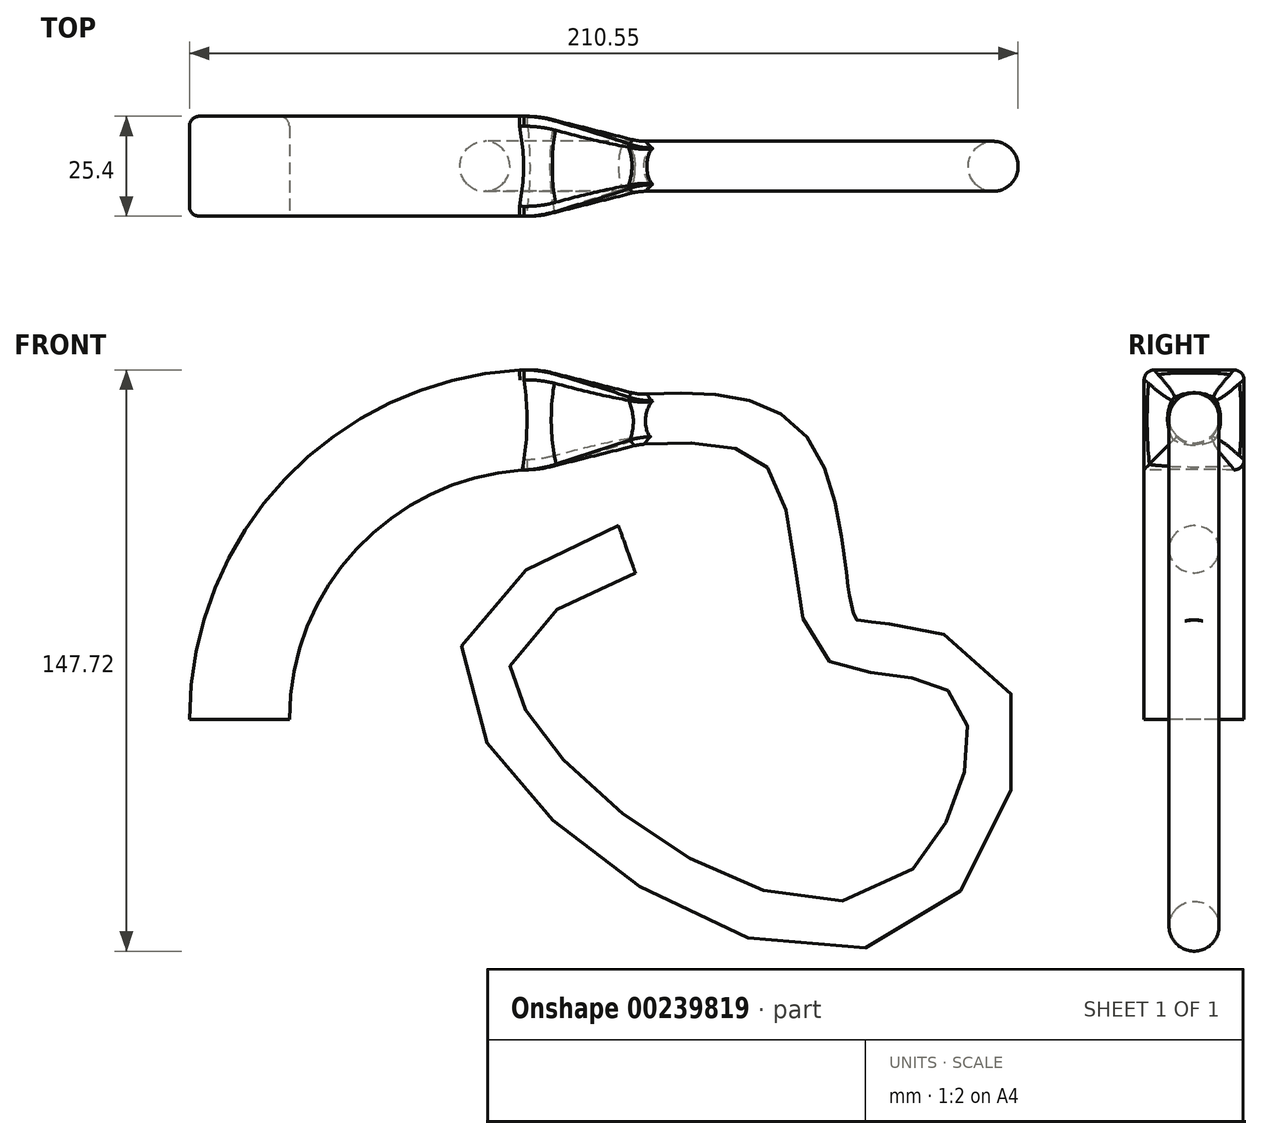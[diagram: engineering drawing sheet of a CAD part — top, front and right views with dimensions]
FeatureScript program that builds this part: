
annotation { "Feature Type Name" : "Feature", "Feature Type Description" : "" }
export const myFeature = defineFeature(function(context is Context, id is Id, definition is map)
    precondition{}
    {
        {
            var Q0;
            Q0=qCreatedBy(makeId("Top.planeOp"),FACE);
            var sketch = newSketch(context, id + "F0", { "sketchPlane" : qUnion([Q0])});
            skLineSegment(sketch, "E0.bottom", {"start": v(12.7, 12.7) * mm, "end": v(-12.7, 12.7) * mm});
            skLineSegment(sketch, "E0.top", {"start": v(12.7, -12.7) * mm, "end": v(-12.7, -12.7) * mm});
            skLineSegment(sketch, "E0.left", {"start": v(12.7, 12.7) * mm, "end": v(12.7, -12.7) * mm});
            skLineSegment(sketch, "E0.right", {"start": v(-12.7, 12.7) * mm, "end": v(-12.7, -12.7) * mm});
            skPoint(sketch, "E0.middle", {"position": v(0, 0) * mm});
            skSolve(sketch);
        }
        {
            var Q0;
            Q0=qCreatedBy(makeId("Front.planeOp"),FACE);
            var sketch = newSketch(context, id + "F1", { "sketchPlane" : qUnion([Q0])});
            skArc(sketch, "E1", {"start": v(76.2, 76.2) * mm, "mid": v(22.32, 53.88) * mm, "end": v(0, 0) * mm});
            skLineSegment(sketch, "E2", {"start": v(0, 0) * mm, "end": v(76.2, 0) * mm, "construction": true});
            skLineSegment(sketch, "E3", {"start": v(76.2, 76.2) * mm, "end": v(76.2, 0) * mm, "construction": true});
            skSolve(sketch);
        }
        {
            var Q0;
            Q0=makeQuery(id+"F0.imprint","IMPRINT",FACE,{"disambiguationData":[TD([[makeQuery(id+"F0.imprint","IMPRINT",EDGE,{"derivedFrom":sQuery(id+"F0.wireOp",EDGE,"E0.bottom")}),1.0]])]});
            var Q1;
            Q1=sQuery(id+"F1.wireOp",EDGE,"E1");
            sweep(context, id + "F2", {"profiles" : qUnion([Q0]), "path" : qUnion([Q1])});
        }
        {
            var Q0;
            Q0=makeQuery(id+"F2.opSweep","CAP_FACE",FACE,{"disambiguationData":[OSD([sQuery(id+"F0.wireOp",EDGE,"E0.bottom"),sQuery(id+"F0.wireOp",EDGE,"E0.top"),sQuery(id+"F0.wireOp",EDGE,"E0.left"),sQuery(id+"F0.wireOp",EDGE,"E0.right"),sQuery(id+"F1.wireOp",VERTEX,"E1.start")])],"isStart":false});
            cPlane(context, id + "F3", {"entities" : qUnion([Q0]), "cplaneType" : CPlaneType.OFFSET, "offset" : 25.4 * mm, "width" : 152.4 * mm, "height" : 152.4 * mm});
        }
        {
            var Q0;
            Q0=qCreatedBy(id+"F3.planeOp",FACE);
            var sketch = newSketch(context, id + "F4", { "sketchPlane" : qUnion([Q0])});
            skCircle(sketch, "E4", {"center": v(0, 76.2) * mm, "radius": 6.35 * mm});
            skLineSegment(sketch, "E5", {"start": v(0, 76.2) * mm, "end": v(12.7, 76.2) * mm, "construction": true});
            skLineSegment(sketch, "E6", {"start": v(0, 76.2) * mm, "end": v(0, 88.9) * mm, "construction": true});
            skSolve(sketch);
        }
        {
            var Q0;
            Q0=makeQuery(id+"F2.opSweep","CAP_FACE",FACE,{"disambiguationData":[OSD([sQuery(id+"F0.wireOp",EDGE,"E0.bottom"),sQuery(id+"F0.wireOp",EDGE,"E0.top"),sQuery(id+"F0.wireOp",EDGE,"E0.left"),sQuery(id+"F0.wireOp",EDGE,"E0.right"),sQuery(id+"F1.wireOp",VERTEX,"E1.start")])],"isStart":false});
            var sketch = newSketch(context, id + "F5", { "sketchPlane" : qUnion([Q0])});
            skLineSegment(sketch, "E7.0", {"start": v(-12.7, 88.9) * mm, "end": v(-12.7, 63.5) * mm});
            skLineSegment(sketch, "E7.1", {"start": v(12.7, 88.9) * mm, "end": v(-12.7, 88.9) * mm});
            skLineSegment(sketch, "E7.2", {"start": v(12.7, 63.5) * mm, "end": v(12.7, 88.9) * mm});
            skLineSegment(sketch, "E7.3", {"start": v(-12.7, 63.5) * mm, "end": v(12.7, 63.5) * mm});
            skSolve(sketch);
        }
        {
            var Q1;
            Q1=makeQuery(id+"F4.imprint","IMPRINT",FACE,{"disambiguationData":[TD([[makeQuery(id+"F4.imprint","IMPRINT",EDGE,{"derivedFrom":sQuery(id+"F4.wireOp",EDGE,"E4")}),1.0]])]});
            var Q2;
            Q2=makeQuery(id+"F5.imprint","IMPRINT",FACE,{"disambiguationData":[TD([[makeQuery(id+"F5.imprint","IMPRINT",EDGE,{"derivedFrom":sQuery(id+"F5.wireOp",EDGE,"E7.0")}),1.0]])]});
            loft(context, id + "F6", {"operationType" : NewBodyOperationType.ADD, "sheetProfilesArray" : [{ "sheetProfileEntities" : qUnion([Q1]) }, { "sheetProfileEntities" : qUnion([Q2]) }]});
        }
        {
            var Q0;
            Q0=qCreatedBy(makeId("Front.planeOp"),FACE);
            var sketch = newSketch(context, id + "F7", { "sketchPlane" : qUnion([Q0])});
            skFitSpline(sketch, "E8", {"points": [v(101.6, 76.2) * mm, v(139.3, 67.77) * mm, v(150.27, 24.2) * mm, v(159.79, 18.43) * mm, v(188.64, 7.46) * mm, v(172.3, -45.3) * mm, v(105.79, -37.55) * mm, v(62.54, 16.31) * mm, v(98.44, 43.24) * mm], "startDerivative": vector(336.37, 18.88) * mm, "endDerivative": vector(396.87, 168) * mm});
            skSolve(sketch);
        }
        {
            var Q0;
            Q0=makeQuery(id+"F6.opLoft","CAP_FACE",FACE,{"disambiguationData":[OSD([makeQuery(id+"F4.imprint","IMPRINT",FACE,{"disambiguationData":[TD([[makeQuery(id+"F4.imprint","IMPRINT",EDGE,{"derivedFrom":sQuery(id+"F4.wireOp",EDGE,"E4")}),1.0]])]})])],"isStart":true});
            var Q1;
            Q1=sQuery(id+"F7.wireOp",EDGE,"E8");
            sweep(context, id + "F8", {"operationType" : NewBodyOperationType.ADD, "profiles" : qUnion([Q0]), "path" : qUnion([Q1])});
        }
        {
            var Q0;
            {var subQ0=sQuery(id+"F5.wireOp",EDGE,"E7.3");var subQ1=sQuery(id+"F5.wireOp",EDGE,"E7.1");var subQ2=sQuery(id+"F5.wireOp",EDGE,"E7.0");var subQ3=sQuery(id+"F4.wireOp",EDGE,"E4");Q0=makeQuery(id+"F8.boolean.opBoolean","MERGE",EDGE,{"derivedFrom":[makeQuery(id+"F6.opLoft","MID_CAP_EDGE",EDGE,{"disambiguationData":[OSD([subQ3,subQ2,subQ1,subQ0])],"capPos":0.0}),makeQuery(id+"F8.opSweep","CAP_EDGE",EDGE,{"disambiguationData":[OSD([subQ3,subQ2,subQ1,subQ0,sQuery(id+"F7.wireOp",VERTEX,"E8.start")])],"isStart":true})]});}
            var Q1;
            {var subQ0=sQuery(id+"F5.wireOp",EDGE,"E7.3");var subQ1=sQuery(id+"F5.wireOp",EDGE,"E7.2");var subQ2=sQuery(id+"F5.wireOp",EDGE,"E7.0");var subQ3=sQuery(id+"F4.wireOp",EDGE,"E4");Q1=makeQuery(id+"F8.boolean.opBoolean","MERGE",EDGE,{"derivedFrom":[makeQuery(id+"F6.opLoft","MID_CAP_EDGE",EDGE,{"disambiguationData":[OSD([subQ3,subQ2,subQ1,subQ0])],"capPos":0.0}),makeQuery(id+"F8.opSweep","CAP_EDGE",EDGE,{"disambiguationData":[OSD([subQ3,subQ2,subQ1,subQ0,sQuery(id+"F7.wireOp",VERTEX,"E8.start")])],"isStart":true})]});}
            var Q2;
            {var subQ0=sQuery(id+"F5.wireOp",EDGE,"E7.3");var subQ1=sQuery(id+"F5.wireOp",EDGE,"E7.2");var subQ2=sQuery(id+"F4.wireOp",EDGE,"E4");Q2=makeQuery(id+"F8.boolean.opBoolean","MERGE",EDGE,{"derivedFrom":[makeQuery(id+"F6.opLoft","MID_CAP_EDGE",EDGE,{"disambiguationData":[OSD([subQ2,subQ1,subQ0])],"capPos":0.0}),makeQuery(id+"F8.opSweep","CAP_EDGE",EDGE,{"disambiguationData":[OSD([subQ2,subQ1,subQ0,sQuery(id+"F7.wireOp",VERTEX,"E8.start")])],"isStart":true})]});}
            var Q3;
            {var subQ0=sQuery(id+"F5.wireOp",EDGE,"E7.3");var subQ1=sQuery(id+"F5.wireOp",EDGE,"E7.2");var subQ2=sQuery(id+"F5.wireOp",EDGE,"E7.1");var subQ3=sQuery(id+"F5.wireOp",EDGE,"E7.0");var subQ4=sQuery(id+"F4.wireOp",EDGE,"E4");Q3=makeQuery(id+"F8.boolean.opBoolean","MERGE",EDGE,{"derivedFrom":[makeQuery(id+"F6.opLoft","MID_CAP_EDGE",EDGE,{"disambiguationData":[OSD([subQ4,subQ3,subQ2,subQ1,subQ0])],"capPos":0.0}),makeQuery(id+"F8.opSweep","CAP_EDGE",EDGE,{"disambiguationData":[OSD([subQ4,subQ3,subQ2,subQ1,subQ0,sQuery(id+"F7.wireOp",VERTEX,"E8.start")])],"isStart":true})]});}
            fillet(context, id + "F9", {"entities" : qUnion([Q0, Q1, Q2, Q3]), "radius" : 12.7 * mm, "tangentPropagation" : true, "allowEdgeOverflow" : false});
        }
        {
            var Q0;
            Q0=makeQuery(id+"F6.boolean.opBoolean","MERGE",EDGE,{"derivedFrom":[makeQuery(id+"F2.opSweep","CAP_EDGE",EDGE,{"disambiguationData":[OSD([sQuery(id+"F0.wireOp",EDGE,"E0.top"),sQuery(id+"F1.wireOp",VERTEX,"E1.start")])],"isStart":false}),makeQuery(id+"F6.opLoft","MID_CAP_EDGE",EDGE,{"disambiguationData":[OSD([sQuery(id+"F5.wireOp",EDGE,"E7.0"),sQuery(id+"F5.wireOp",EDGE,"E7.1"),sQuery(id+"F5.wireOp",EDGE,"E7.3")])],"capPos":1.0})]});
            var Q1;
            Q1=makeQuery(id+"F6.boolean.opBoolean","MERGE",EDGE,{"derivedFrom":[makeQuery(id+"F2.opSweep","CAP_EDGE",EDGE,{"disambiguationData":[OSD([sQuery(id+"F0.wireOp",EDGE,"E0.right"),sQuery(id+"F1.wireOp",VERTEX,"E1.start")])],"isStart":false}),makeQuery(id+"F6.opLoft","MID_CAP_EDGE",EDGE,{"disambiguationData":[OSD([sQuery(id+"F5.wireOp",EDGE,"E7.0"),sQuery(id+"F5.wireOp",EDGE,"E7.1"),sQuery(id+"F5.wireOp",EDGE,"E7.2")])],"capPos":1.0})]});
            var Q2;
            Q2=makeQuery(id+"F6.boolean.opBoolean","MERGE",EDGE,{"derivedFrom":[makeQuery(id+"F2.opSweep","CAP_EDGE",EDGE,{"disambiguationData":[OSD([sQuery(id+"F0.wireOp",EDGE,"E0.bottom"),sQuery(id+"F1.wireOp",VERTEX,"E1.start")])],"isStart":false}),makeQuery(id+"F6.opLoft","MID_CAP_EDGE",EDGE,{"disambiguationData":[OSD([sQuery(id+"F5.wireOp",EDGE,"E7.1"),sQuery(id+"F5.wireOp",EDGE,"E7.2"),sQuery(id+"F5.wireOp",EDGE,"E7.3")])],"capPos":1.0})]});
            var Q3;
            Q3=makeQuery(id+"F6.boolean.opBoolean","MERGE",EDGE,{"derivedFrom":[makeQuery(id+"F2.opSweep","CAP_EDGE",EDGE,{"disambiguationData":[OSD([sQuery(id+"F0.wireOp",EDGE,"E0.left"),sQuery(id+"F1.wireOp",VERTEX,"E1.start")])],"isStart":false}),makeQuery(id+"F6.opLoft","MID_CAP_EDGE",EDGE,{"disambiguationData":[OSD([sQuery(id+"F5.wireOp",EDGE,"E7.0"),sQuery(id+"F5.wireOp",EDGE,"E7.2"),sQuery(id+"F5.wireOp",EDGE,"E7.3")])],"capPos":1.0})]});
            fillet(context, id + "F10", {"entities" : qUnion([Q0, Q1, Q2, Q3]), "radius" : 25.4 * mm, "tangentPropagation" : true, "allowEdgeOverflow" : false});
        }
        {
            var Q0;
            Q0=makeQuery(id+"F6.opLoft","SWEPT_EDGE",EDGE,{"disambiguationData":[OSD([sQuery(id+"F4.wireOp",EDGE,"E4"),sQuery(id+"F5.wireOp",EDGE,"E7.0"),sQuery(id+"F5.wireOp",EDGE,"E7.2"),sQuery(id+"F5.wireOp",EDGE,"E7.3")])]});
            var Q1;
            Q1=makeQuery(id+"F6.opLoft","SWEPT_EDGE",EDGE,{"disambiguationData":[OSD([sQuery(id+"F4.wireOp",EDGE,"E4"),sQuery(id+"F5.wireOp",EDGE,"E7.0"),sQuery(id+"F5.wireOp",EDGE,"E7.1"),sQuery(id+"F5.wireOp",EDGE,"E7.3")])]});
            var Q2;
            Q2=makeQuery(id+"F6.opLoft","SWEPT_EDGE",EDGE,{"disambiguationData":[OSD([sQuery(id+"F4.wireOp",EDGE,"E4"),sQuery(id+"F5.wireOp",EDGE,"E7.0"),sQuery(id+"F5.wireOp",EDGE,"E7.1"),sQuery(id+"F5.wireOp",EDGE,"E7.2")])]});
            var Q3;
            Q3=makeQuery(id+"F6.opLoft","SWEPT_EDGE",EDGE,{"disambiguationData":[OSD([sQuery(id+"F5.wireOp",EDGE,"E7.2"),sQuery(id+"F5.wireOp",EDGE,"E7.3")])]});
            fillet(context, id + "F11", {"entities" : qUnion([Q0, Q1, Q2, Q3]), "radius" : 2.54 * mm, "tangentPropagation" : true, "allowEdgeOverflow" : false});
        }
    });
